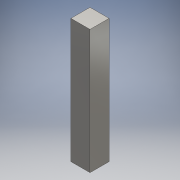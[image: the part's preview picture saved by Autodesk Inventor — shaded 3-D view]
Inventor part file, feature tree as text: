
AUTODESK INVENTOR PART (.ipt)
format: ipt  version: 2016 (Build 200138000, 138)  size: 88,576 bytes
history: native  units: mm
features: extrude x1, sketch x1
ambient origin geometry x8: Origin, YZ Plane, XZ Plane, XY Plane, X Axis, Y Axis, Z Axis, Center Point
bodies: Solid1 (feature_tree)
feature tree (2):
  extrude  "Extrusion1"  Depth=1300.0mm
  sketch  "Sketch1"  dims[d0=200.0mm d1=1300.0mm d2=200.0mm d3=0.0mm]
